# Revit family: 2070130(n0300)
name_source: partatom
category: Security Devices
units: mm (PartAtom-declared; Revit-internal decimal feet)

## family parameters
Always vertical = No
Cut with Voids When Loaded = No
Host = Ceiling
OmniClass Number = 23.85.30.14
OmniClass Title = Presence Detection/Registration
Room Calculation Point = No
Shared = Yes

## types (2) — shared parameters
zero-valued in all types: A

## per-type parameters (varying)
- Type 1: CTN=0; EF000008=0 mm  [stored 0 ft]; EF000040=0 mm  [stored 0 ft]; EF000049=0 mm  [stored 0 ft]; EF000218=0 mm  [stored 0 ft]; EF000551=0 mm  [stored 0 ft]; EF000846=0 mm  [stored 0 ft]; EF000943=0 mm  [stored 0 ft]; EF001322=0 mm  [stored 0 ft]; EF001323=0 mm  [stored 0 ft]; EF003843=0 mm  [stored 0 ft]; EF003882=0; EF004101=0.00°; EF004265=0 mm  [stored 0 ft]; EF008011=0 mm  [stored 0 ft]; EF010517=0 mm  [stored 0 ft]; EF010886=0 mm  [stored 0 ft]; EF010945=0 mm  [stored 0 ft]; EF010946=0 mm  [stored 0 ft]; EF012278=0 mm  [stored 0 ft]; EF012569=0; LOG=0; NOCUPEROU=0; PRICEQUANTITY=0; QUANTITYINT=0; QUANTITYMIN=0
- 2070130: ARTICLENO=NB; BOMINFO=LINA; CATALOG=Theben; COO=HU; CTN=90314990; DEEPLINK_PRODUKTSEITE=http://www.theben.de; DESCLONG=Slave presence detector for ceiling mounting, extended detection area square, can only be used as master in combination with thePrema; DESCSHORT=Presence detector for ceiling mounting, slave version; EF000003=EV000383; EF000007=White; EF000008=110 mm  [stored 0.360892 ft]; EF000010=Presence detector; EF000025=false; EF000040=82 mm  [stored 0.269029 ft]; EF000049=110 mm  [stored 0.360892 ft]; EF000124=Screw clamp; EF000139=Untreated; EF000147=false; EF000187=AC; EF000218=40 mm  [stored 0.131234 ft]; EF000416=50, 60 Hz; EF000483=false; EF000551=110 mm  [stored 0.360892 ft]; EF000846=48 mm  [stored 0.15748 ft]; EF000943=48 mm  [stored 0.15748 ft]; EF001098=true; EF001099=false; EF001198=false; EF001257=Thermoplast; EF001322=5000 mm; EF001323=5000 mm; EF001731=0, 50 °C; EF002169=Plastic; EF003429=false; EF003808=false; EF003832=false; EF003843=10000 mm; EF003848=false; EF003858=false; EF003863=false; EF003882=9010; EF003890=false; EF003898=false; EF003904=true; EF003920=false; EF004101=360.00°; EF004265=48 mm  [stored 0.15748 ft]; EF004293=IK04; EF005474=IP40; EF005624=false; EF006243=false; EF006311=false; EF006569=matt; EF006582=0, 360 °; EF006644=false; EF007575=false; EF008011=2500 mm  [stored 8.2021 ft]; EF009569=false; EF010517=42 mm  [stored 0.137795 ft]; EF010886=20 mm  [stored 0.0656168 ft]; EF010945=110 mm  [stored 0.360892 ft]; EF010946=65 mm  [stored 0.213255 ft]; EF011072=false; EF011991=false; EF012278=46 mm  [stored 0.150919 ft]; EF012569=64; EF014925=false; EF014926=false; EF014927=false; EF020270=Passive infrared; EF021180=true; EF023790=false; GEBRAUCHSANLEITUNG=http://www.theben.de; INTNO=7612748005624; LINA=2070130; LOG=300; MANUID=2070130; MANUNAME=Theben AG; MANUTYPEDESC=thePrema P360 Slave E UP WH; Manufacturer=Theben; Model=2070130; NB=2070130(N0300); NBSYN=$MANUID.($SA.$A.$LOG.); NN=thePrema P; NOCUPEROU=1; PRICEQUANTITY=1; PRODUKTDATENBLATT=http://www.theben.de; QUANTITYINT=1; QUANTITYMIN=1; REACH_ERKLAERUNG=http://www.theben.de; REMARKS=ERP-GROUP 340; SA=None; SUPPLIER=THEBEN; SUPPLIERALTNO=2070130

note: [stored X ft] marks values corroborated as IEEE doubles in the binary element streams (Revit-internal decimal feet)

## geometry (parser evidence)
native form markers: Sweep x10
no freeform markers — native parametric forms only
